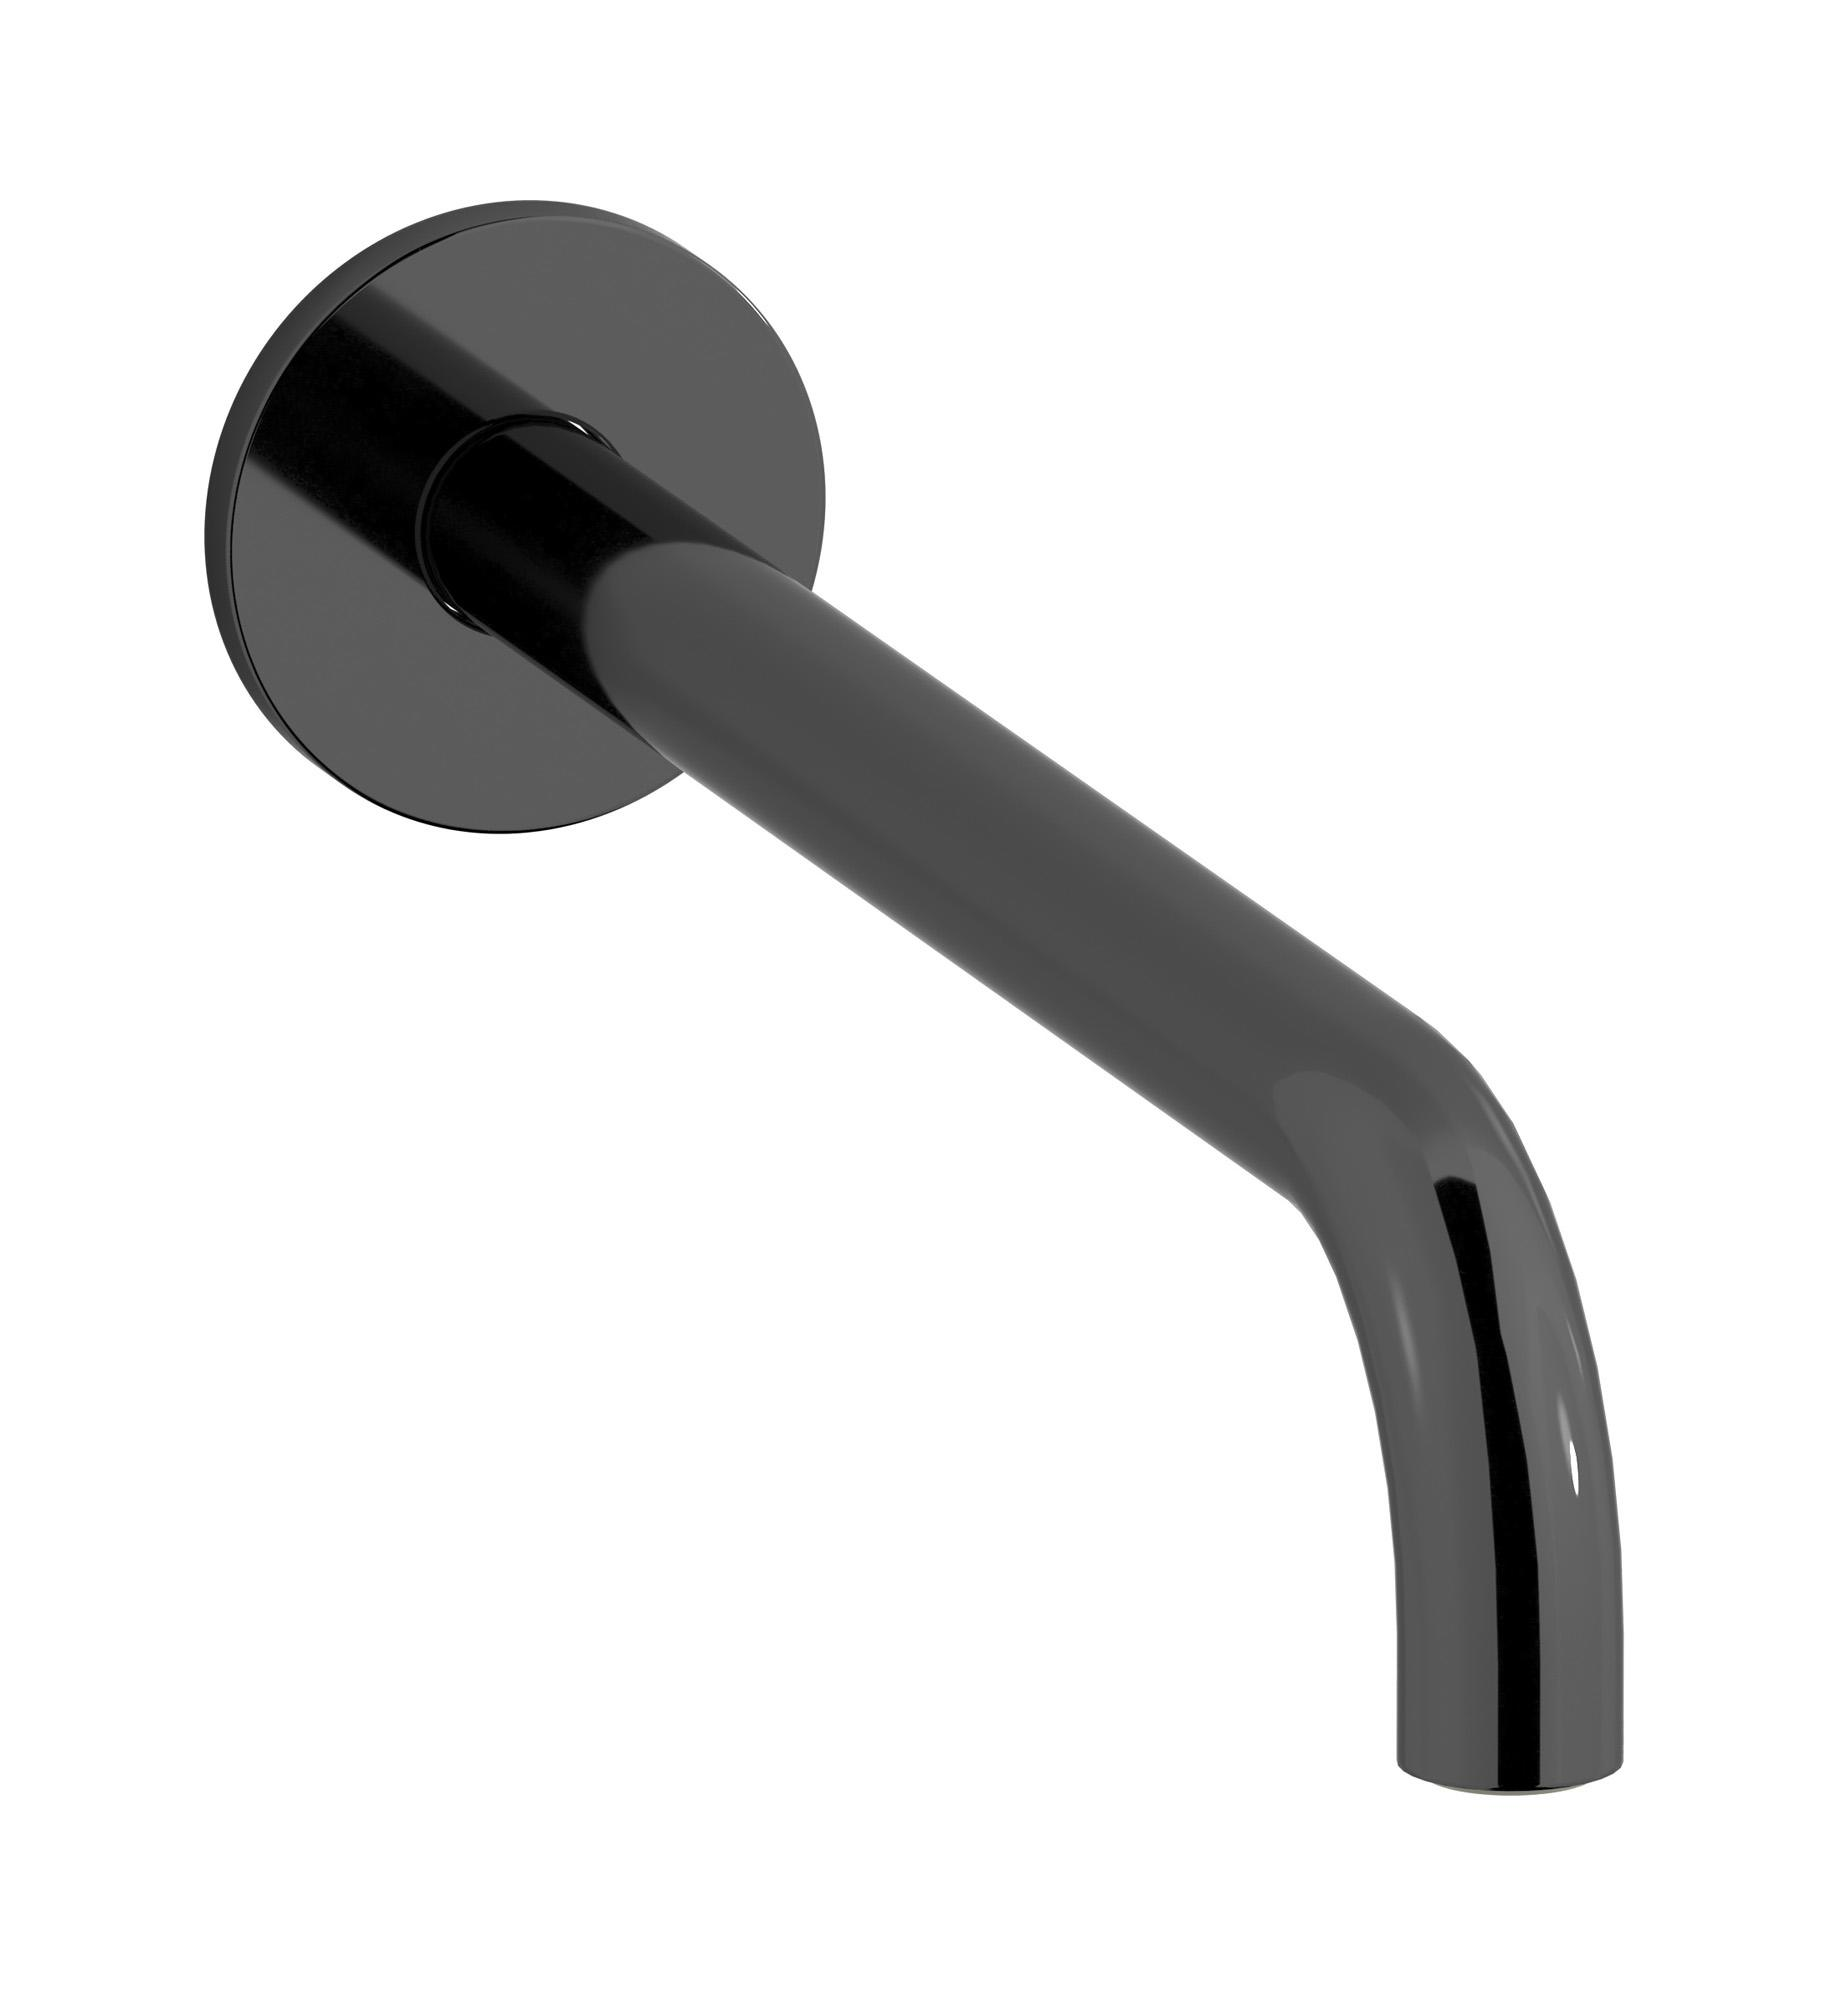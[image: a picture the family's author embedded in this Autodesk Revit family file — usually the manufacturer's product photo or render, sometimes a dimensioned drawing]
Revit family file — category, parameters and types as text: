
# Revit family: RX328
name_source: partatom
category: Apparecchi idraulici
units: mm (PartAtom-declared; Revit-internal decimal feet)

## family parameters
Basato su piano di lavoro = No
Condiviso = No
Mantieni orientamento annotazione = No
Numero OmniClass = 23.45.55.17
Punto di calcolo locali = No
Quota connettore circolare = Usa diametro
Sempre verticale = Sì
Taglio con vuoti quando caricato = No
Tipo di parte = Normale
Titolo OmniClass = Mixing Faucets

## types (12) — shared parameters
Commenti sul tipo = Long wall mounted spout
Connessione CW = No
Connessione HW = No
Connessione di scarico = No
Connessione di ventilazione = No
Descrizione = Long wall mounted spout
Produttore = IB Rubinetterie S.p.A.
URL = https://www.weareib.it
Water inlet = 10 mm  [stored 0.0328084 ft]
zero-valued in all types: Prospetto di default

## per-type parameters (varying)
| type | Finishes surface | Immagine tipo | Modello |
| Chrome | IB_Chrome | RX328CC.jpg | RX328CC |
| Black Chrome | IB_Black chrome | RX328CF.jpg | RX328CF |
| Brushed Black Chrome | IB_Brushed black chrome | RX328CS.jpg | RX328CS |
| Pale Gold | IB_Pale gold | RX328II.jpg | RX328II |
| Brushed Pale Gold | IB_brushed pale gold | RX328IS.jpg | RX328IS |
| Matt Black | IB_matt black | RX328NP.jpg | RX328NP |
| Natural Brass | IB_Brass | RX328ON.jpg | RX328ON |
| Gold | IB_gold | RX328OO.jpg | RX328OO |
| Brushed Gold | IB_brushed gold | RX328OS.jpg | RX328OS |
| Rose Gold | IB_Rose gold | RX328RS.jpg | RX328RS |
| Brushed Rose Gold | IB_Brushed rose gold | RX328SR.jpg | RX328SR |
| Brushed Nickel | IB_Brushed nickel | RX328SS.jpg | RX328SS |

note: [stored X ft] marks values corroborated as IEEE doubles in the binary element streams (Revit-internal decimal feet)
